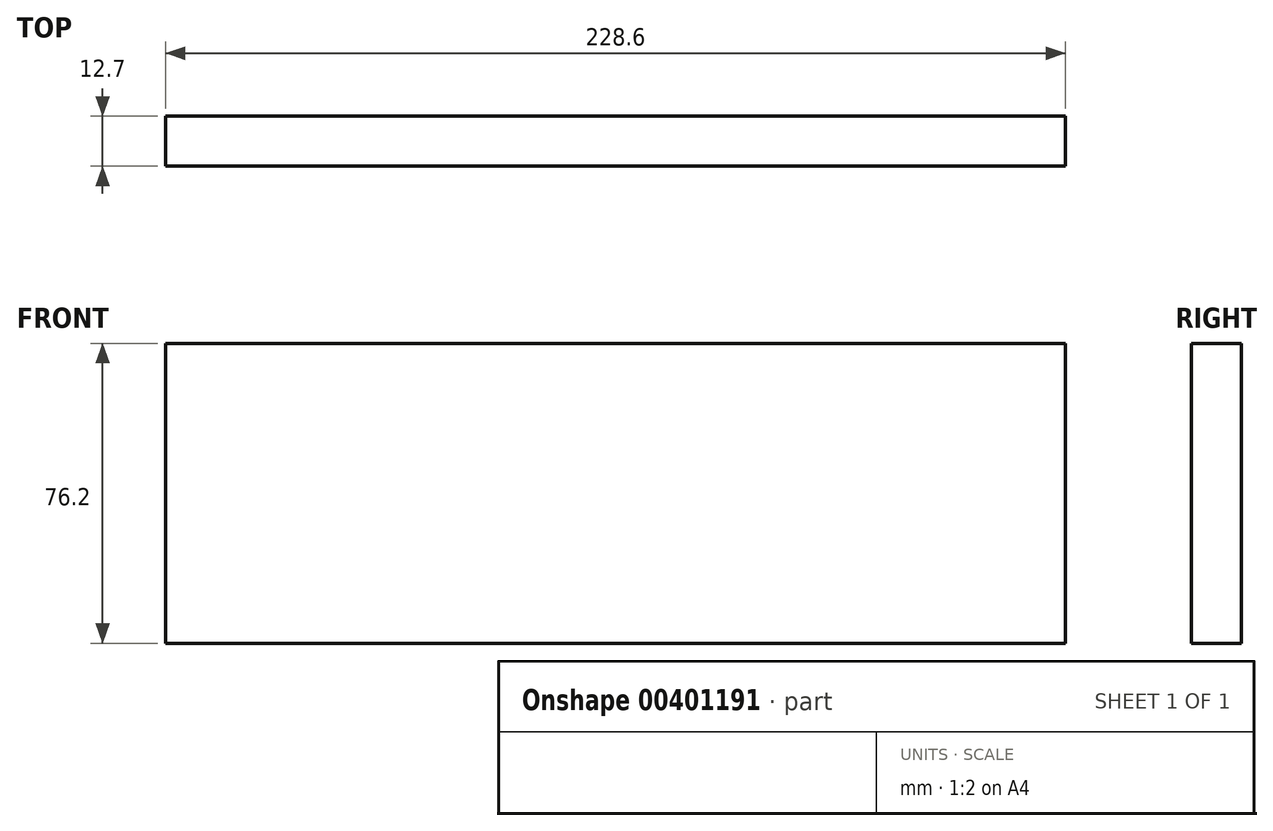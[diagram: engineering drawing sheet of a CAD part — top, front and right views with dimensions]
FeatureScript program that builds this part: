
annotation { "Feature Type Name" : "Feature", "Feature Type Description" : "" }
export const myFeature = defineFeature(function(context is Context, id is Id, definition is map)
    precondition{}
    {
        {
            var Q0;
            Q0=qCreatedBy(makeId("Front.planeOp"),FACE);
            var sketch = newSketch(context, id + "F0", { "sketchPlane" : qUnion([Q0])});
            skLineSegment(sketch, "E0.bottom", {"start": v(0, 0) * mm, "end": v(-228.6, 0) * mm});
            skLineSegment(sketch, "E0.top", {"start": v(0, 76.2) * mm, "end": v(-228.6, 76.2) * mm});
            skLineSegment(sketch, "E0.left", {"start": v(0, 0) * mm, "end": v(0, 76.2) * mm});
            skLineSegment(sketch, "E0.right", {"start": v(-228.6, 0) * mm, "end": v(-228.6, 76.2) * mm});
            skSolve(sketch);
        }
        {
            var Q0;
            Q0=makeQuery(id+"F0.imprint","IMPRINT",FACE,{"disambiguationData":[TD([[makeQuery(id+"F0.imprint","IMPRINT",EDGE,{"derivedFrom":sQuery(id+"F0.wireOp",EDGE,"E0.bottom")}),-1.0]])]});
            extrude(context, id + "F1", {"entities" : qUnion([Q0]), "depth" : 12.7 * mm});
        }
    });
